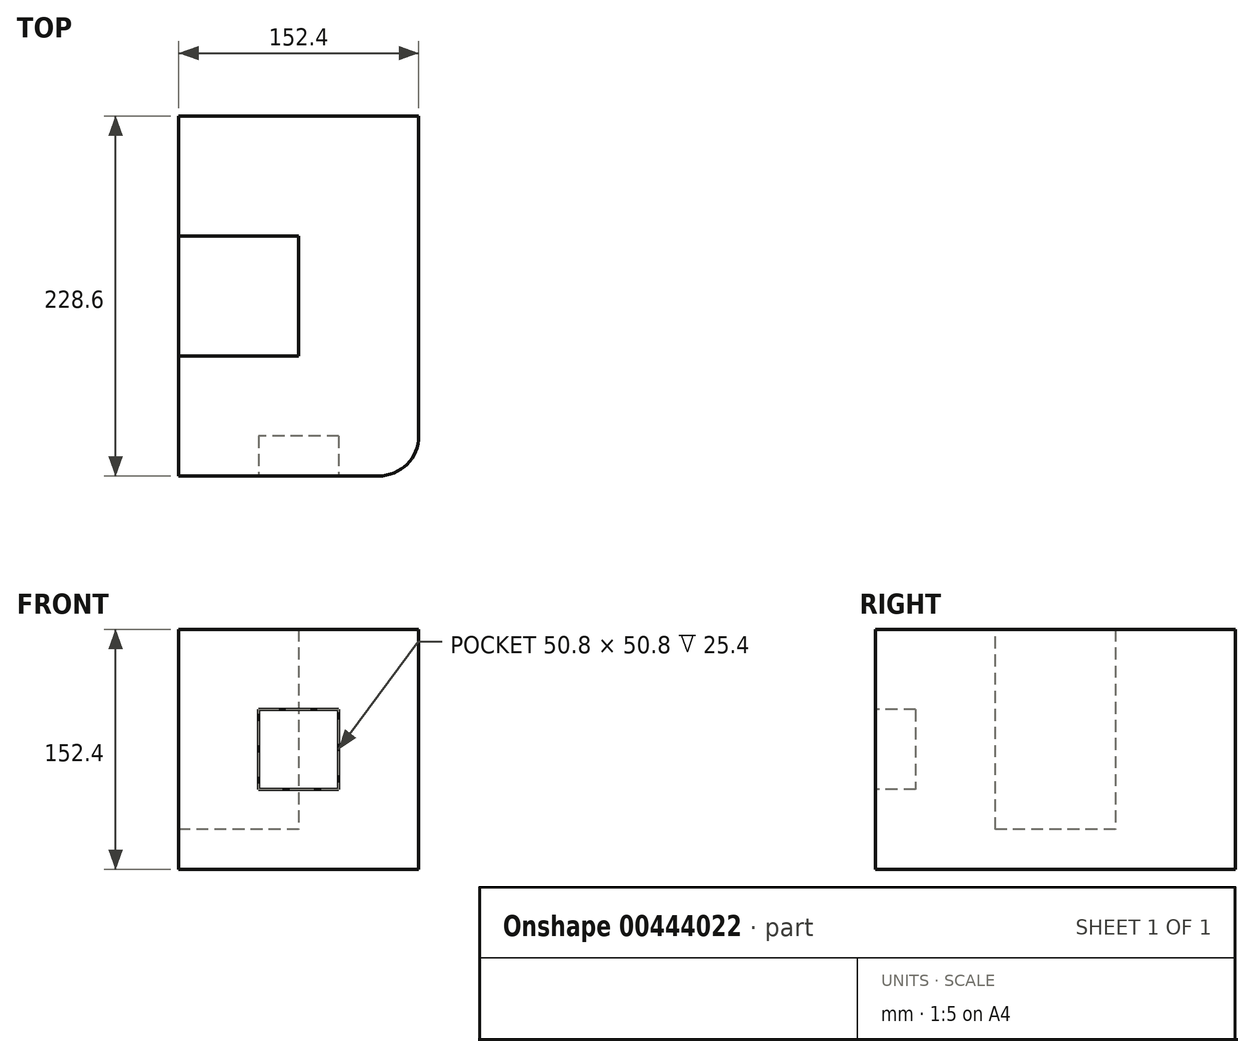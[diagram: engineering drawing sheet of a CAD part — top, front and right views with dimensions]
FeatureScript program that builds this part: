
annotation { "Feature Type Name" : "Feature", "Feature Type Description" : "" }
export const myFeature = defineFeature(function(context is Context, id is Id, definition is map)
    precondition{}
    {
        {
            var Q0;
            Q0=qCreatedBy(makeId("Right.planeOp"),FACE);
            var sketch = newSketch(context, id + "F0", { "sketchPlane" : qUnion([Q0])});
            skLineSegment(sketch, "E0", {"start": v(0, 0) * mm, "end": v(-228.6, 0) * mm});
            skLineSegment(sketch, "E1", {"start": v(-228.6, 0) * mm, "end": v(-228.6, 152.4) * mm});
            skLineSegment(sketch, "E2", {"start": v(-228.6, 152.4) * mm, "end": v(0, 152.4) * mm});
            skLineSegment(sketch, "E3", {"start": v(0, 152.4) * mm, "end": v(0, 0) * mm});
            skSolve(sketch);
        }
        {
            var Q0;
            Q0=makeQuery(id+"F0.imprint","IMPRINT",FACE,{"disambiguationData":[TD([[makeQuery(id+"F0.imprint","IMPRINT",EDGE,{"derivedFrom":sQuery(id+"F0.wireOp",EDGE,"E0")}),-1.0]])]});
            extrude(context, id + "F1", {"entities" : qUnion([Q0]), "endBound" : BoundingType.SYMMETRIC, "depth" : 152.4 * mm});
        }
        {
            var Q0;
            Q0=makeQuery(id+"F1.opExtrude","CAP_FACE",FACE,{"disambiguationData":[OSD([sQuery(id+"F0.wireOp",EDGE,"E0"),sQuery(id+"F0.wireOp",EDGE,"E1"),sQuery(id+"F0.wireOp",EDGE,"E2"),sQuery(id+"F0.wireOp",EDGE,"E3")])],"isStart":true});
            var sketch = newSketch(context, id + "F2", { "sketchPlane" : qUnion([Q0])});
            skLineSegment(sketch, "E4", {"start": v(76.2, 152.4) * mm, "end": v(76.2, 25.4) * mm});
            skLineSegment(sketch, "E5", {"start": v(76.2, 25.4) * mm, "end": v(152.4, 25.4) * mm});
            skLineSegment(sketch, "E6", {"start": v(152.4, 25.4) * mm, "end": v(152.4, 152.4) * mm});
            skLineSegment(sketch, "E7", {"start": v(152.4, 152.4) * mm, "end": v(76.2, 152.4) * mm});
            skSolve(sketch);
        }
        {
            var Q0;
            Q0=makeQuery(id+"F2.imprint","IMPRINT",FACE,{"disambiguationData":[TD([[makeQuery(id+"F2.imprint","IMPRINT",EDGE,{"derivedFrom":sQuery(id+"F2.wireOp",EDGE,"E4")}),1.0]])]});
            extrude(context, id + "F3", {"entities" : qUnion([Q0]), "operationType" : NewBodyOperationType.REMOVE, "oppositeDirection" : true, "depth" : 76.2 * mm});
        }
        {
            var Q0;
            Q0=makeQuery(id+"F1.opExtrude","CAP_EDGE",EDGE,{"disambiguationData":[OSD([sQuery(id+"F0.wireOp",EDGE,"E1")])],"isStart":false});
            fillet(context, id + "F4", {"entities" : qUnion([Q0]), "radius" : 25.4 * mm, "tangentPropagation" : true, "allowEdgeOverflow" : false});
        }
        {
            var Q0;
            Q0=makeQuery(id+"F1.opExtrude","SWEPT_FACE",FACE,{"disambiguationData":[OSD([sQuery(id+"F0.wireOp",EDGE,"E1")])]});
            var sketch = newSketch(context, id + "F5", { "sketchPlane" : qUnion([Q0])});
            skLineSegment(sketch, "E8", {"start": v(-25.4, 101.6) * mm, "end": v(-25.4, 50.8) * mm});
            skLineSegment(sketch, "E9", {"start": v(-25.4, 50.8) * mm, "end": v(25.4, 50.8) * mm});
            skLineSegment(sketch, "E10", {"start": v(25.4, 50.8) * mm, "end": v(25.4, 101.6) * mm});
            skLineSegment(sketch, "E11", {"start": v(25.4, 101.6) * mm, "end": v(-25.4, 101.6) * mm});
            skSolve(sketch);
        }
        {
            var Q0;
            Q0=makeQuery(id+"F5.imprint","IMPRINT",FACE,{"disambiguationData":[TD([[makeQuery(id+"F5.imprint","IMPRINT",EDGE,{"derivedFrom":sQuery(id+"F5.wireOp",EDGE,"E8")}),1.0]])]});
            extrude(context, id + "F6", {"entities" : qUnion([Q0]), "operationType" : NewBodyOperationType.REMOVE, "oppositeDirection" : true, "depth" : 25.4 * mm});
        }
    });
